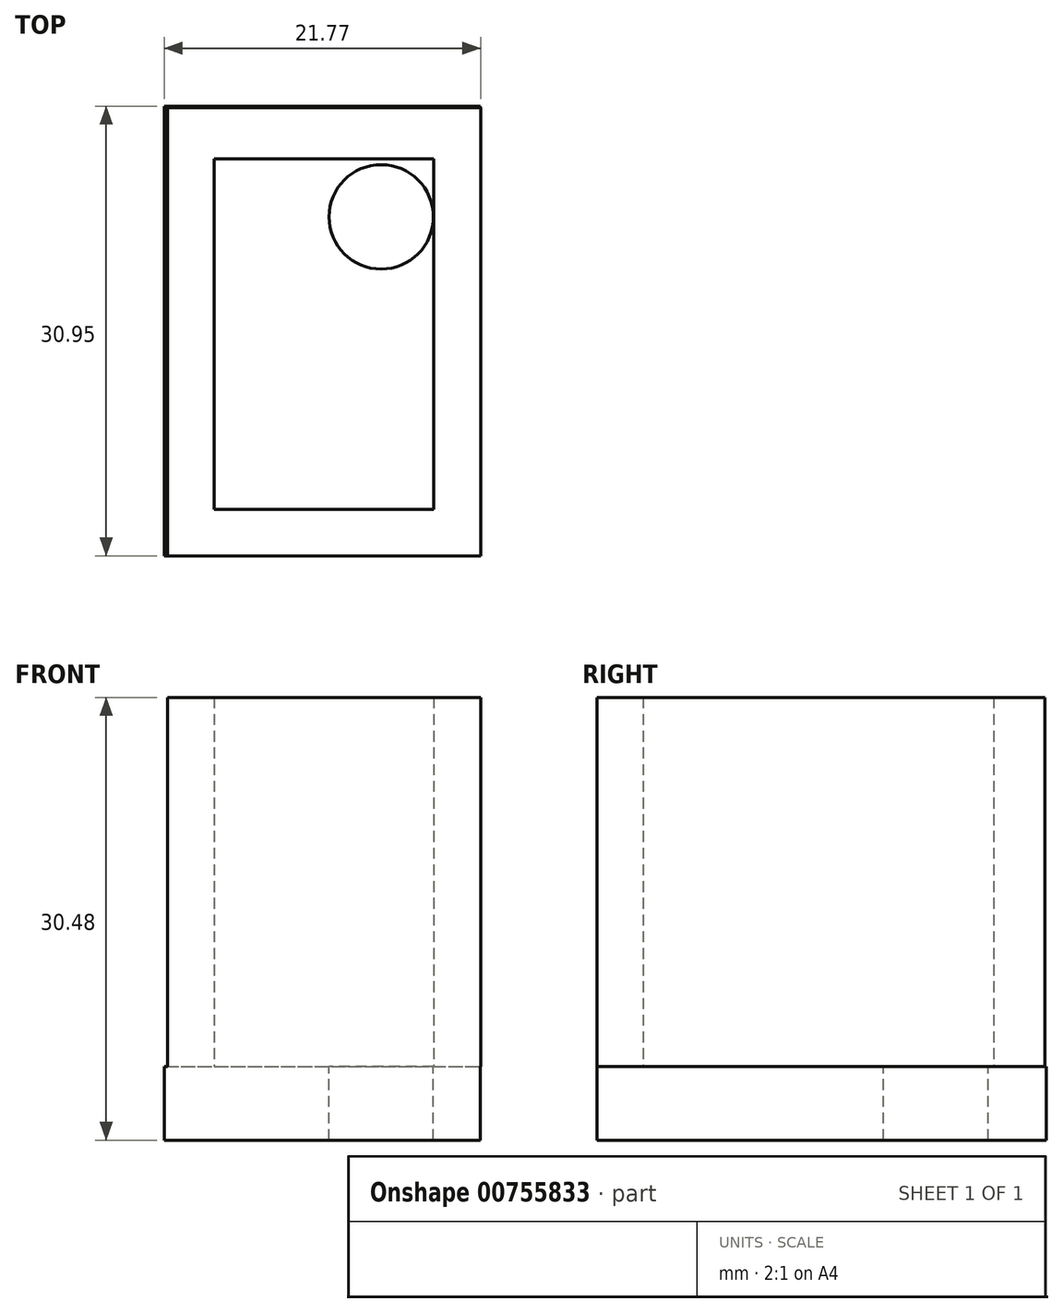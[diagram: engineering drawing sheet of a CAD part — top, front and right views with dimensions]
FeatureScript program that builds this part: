
annotation { "Feature Type Name" : "Feature", "Feature Type Description" : "" }
export const myFeature = defineFeature(function(context is Context, id is Id, definition is map)
    precondition{}
    {
        {
            var Q0;
            Q0=qCreatedBy(makeId("Top.planeOp"),FACE);
            var sketch = newSketch(context, id + "F0", { "sketchPlane" : qUnion([Q0])});
            skLineSegment(sketch, "E0.bottom", {"start": v(-14.18, -12.73) * mm, "end": v(0.93, -12.73) * mm});
            skLineSegment(sketch, "E0.top", {"start": v(-14.18, 11.4) * mm, "end": v(0.93, 11.4) * mm});
            skLineSegment(sketch, "E0.left", {"start": v(-14.18, -12.73) * mm, "end": v(-14.18, 11.4) * mm});
            skLineSegment(sketch, "E0.right", {"start": v(0.93, -12.73) * mm, "end": v(0.93, 11.4) * mm});
            skLineSegment(sketch, "E1.bottom", {"start": v(-17.4, 14.9) * mm, "end": v(4.15, 14.9) * mm});
            skLineSegment(sketch, "E1.top", {"start": v(-17.4, -15.93) * mm, "end": v(4.15, -15.93) * mm});
            skLineSegment(sketch, "E1.left", {"start": v(-17.4, 14.9) * mm, "end": v(-17.4, -15.93) * mm});
            skLineSegment(sketch, "E1.right", {"start": v(4.15, 14.9) * mm, "end": v(4.15, -15.93) * mm});
            skSolve(sketch);
        }
        {
            var Q0;
            Q0=makeQuery(id+"F0.imprint","IMPRINT",FACE,{"disambiguationData":[TD([[makeQuery(id+"F0.imprint","IMPRINT",EDGE,{"derivedFrom":sQuery(id+"F0.wireOp",EDGE,"E0.bottom")}),-1.0]])]});
            extrude(context, id + "F1", {"entities" : qUnion([Q0]), "depth" : 25.4 * mm, "offsetDistance" : 25.4 * mm});
        }
        {
            var Q0;
            Q0=qCreatedBy(makeId("Top.planeOp"),FACE);
            var sketch = newSketch(context, id + "F2", { "sketchPlane" : qUnion([Q0])});
            skLineSegment(sketch, "E2.bottom", {"start": v(-17.62, 15.02) * mm, "end": v(4.12, 15.02) * mm});
            skLineSegment(sketch, "E2.top", {"start": v(-17.62, -15.93) * mm, "end": v(4.12, -15.93) * mm});
            skLineSegment(sketch, "E2.left", {"start": v(-17.62, 15.02) * mm, "end": v(-17.62, -15.93) * mm});
            skLineSegment(sketch, "E2.right", {"start": v(4.12, 15.02) * mm, "end": v(4.12, -15.93) * mm});
            skCircle(sketch, "E3", {"center": v(-2.7, 7.4) * mm, "radius": 3.6 * mm});
            skSolve(sketch);
        }
        {
            var Q0;
            Q0=makeQuery(id+"F2.imprint","IMPRINT",FACE,{"disambiguationData":[TD([[makeQuery(id+"F2.imprint","IMPRINT",EDGE,{"derivedFrom":sQuery(id+"F2.wireOp",EDGE,"E2.bottom")}),-1.0]])]});
            extrude(context, id + "F3", {"entities" : qUnion([Q0]), "operationType" : NewBodyOperationType.ADD, "oppositeDirection" : true, "depth" : 5.08 * mm, "offsetDistance" : 25.4 * mm});
        }
    });
